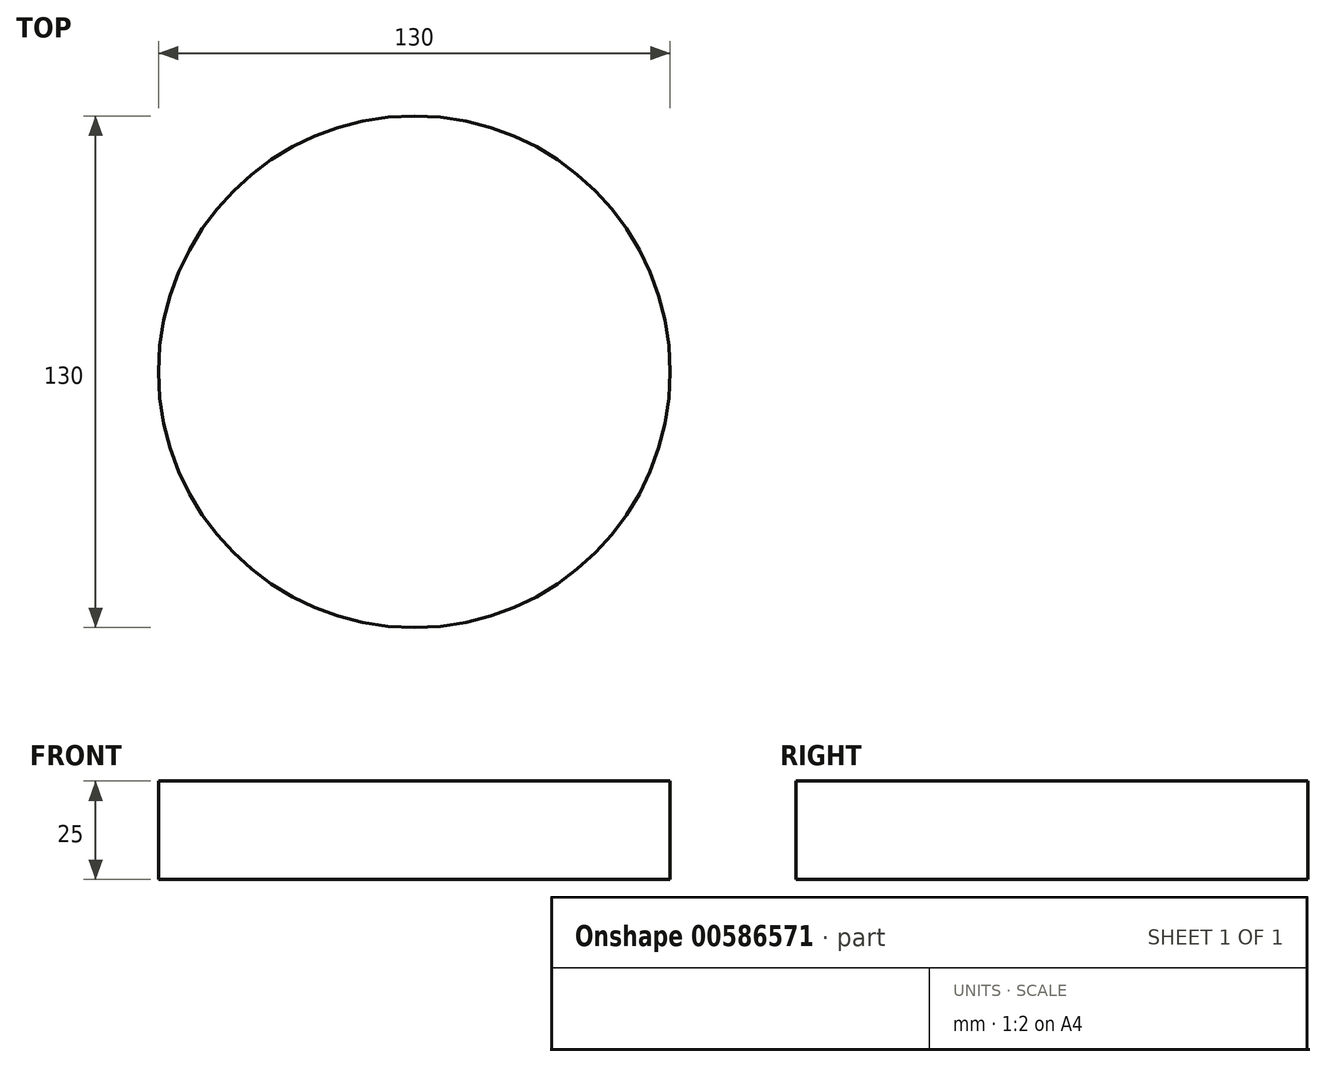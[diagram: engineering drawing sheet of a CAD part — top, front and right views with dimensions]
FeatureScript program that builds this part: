
annotation { "Feature Type Name" : "Feature", "Feature Type Description" : "" }
export const myFeature = defineFeature(function(context is Context, id is Id, definition is map)
    precondition{}
    {
        {
            var Q0;
            Q0=qCreatedBy(makeId("Top.planeOp"),FACE);
            var sketch = newSketch(context, id + "F0", { "sketchPlane" : qUnion([Q0])});
            skCircle(sketch, "E0", {"center": v(0, 0) * mm, "radius": 65 * mm});
            skSolve(sketch);
        }
        {
            var Q0;
            Q0 = qSketchRegion(id + "F0", true);
            var sketch = newSketch(context, id + "F1", { "sketchPlane" : qUnion([Q0])});
            skSolve(sketch);
        }
        {
            var Q0;
            Q0 = qSketchRegion(id + "F1", true);
            var Q1;
            Q1=makeQuery(id+"F0.imprint","IMPRINT",FACE,{"disambiguationData":[TD([[makeQuery(id+"F0.imprint","IMPRINT",EDGE,{"derivedFrom":sQuery(id+"F0.wireOp",EDGE,"E0")}),1.0]])]});
            extrude(context, id + "F2", {"entities" : qUnion([Q0, Q1]), "depth" : 25 * mm, "offsetDistance" : 25 * mm});
        }
    });
